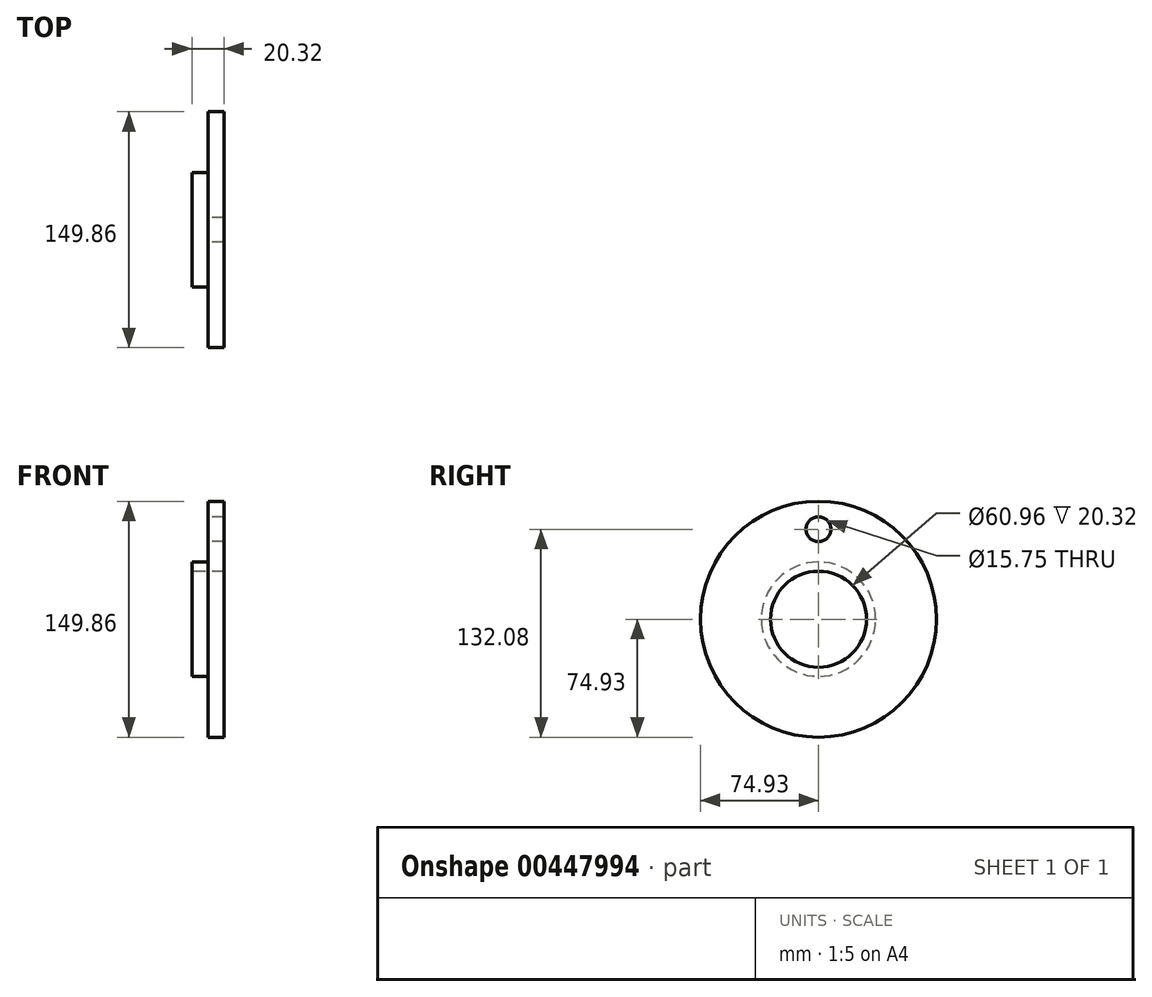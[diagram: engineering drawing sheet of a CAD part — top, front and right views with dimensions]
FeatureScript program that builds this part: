
annotation { "Feature Type Name" : "Feature", "Feature Type Description" : "" }
export const myFeature = defineFeature(function(context is Context, id is Id, definition is map)
    precondition{}
    {
        {
            var Q0;
            Q0=qCreatedBy(makeId("Front.planeOp"),FACE);
            var sketch = newSketch(context, id + "F0", { "sketchPlane" : qUnion([Q0])});
            skLineSegment(sketch, "E0", {"start": v(-98.75, 0) * mm, "end": v(111.7, 0) * mm, "construction": true});
            skSolve(sketch);
        }
        {
            var Q0;
            Q0=qCreatedBy(makeId("Front.planeOp"),FACE);
            var sketch = newSketch(context, id + "F1", { "sketchPlane" : qUnion([Q0])});
            skLineSegment(sketch, "E1", {"start": v(0, 30.48) * mm, "end": v(0, 36.32) * mm});
            skLineSegment(sketch, "E2", {"start": v(0, 36.32) * mm, "end": v(10.16, 36.32) * mm});
            skLineSegment(sketch, "E3", {"start": v(10.16, 36.32) * mm, "end": v(10.16, 74.93) * mm});
            skLineSegment(sketch, "E4", {"start": v(10.16, 74.93) * mm, "end": v(20.32, 74.93) * mm});
            skLineSegment(sketch, "E5", {"start": v(20.32, 74.93) * mm, "end": v(20.32, 30.48) * mm});
            skLineSegment(sketch, "E6", {"start": v(20.32, 30.48) * mm, "end": v(0, 30.48) * mm});
            skSolve(sketch);
        }
        {
            var Q0;
            Q0=makeQuery(id+"F1.imprint","IMPRINT",FACE,{"disambiguationData":[TD([[makeQuery(id+"F1.imprint","IMPRINT",EDGE,{"derivedFrom":sQuery(id+"F1.wireOp",EDGE,"E1")}),-1.0]])]});
            var Q1;
            Q1=sQuery(id+"F0.wireOp",EDGE,"E0");
            revolve(context, id + "F2", {"entities" : qUnion([Q0]), "axis" : qUnion([Q1]), "revolveType" : RevolveType.FULL});
        }
        {
            var Q0;
            Q0=makeQuery(id+"F2.opRevolve","SWEPT_FACE",FACE,{"disambiguationData":[OSD([sQuery(id+"F1.wireOp",EDGE,"E3")])]});
            var sketch = newSketch(context, id + "F3", { "sketchPlane" : qUnion([Q0])});
            skCircle(sketch, "E7", {"center": v(0, 0) * mm, "radius": 57.15 * mm, "construction": true});
            skCircle(sketch, "E8", {"center": v(0, 57.15) * mm, "radius": 7.87 * mm});
            skSolve(sketch);
        }
        {
            var Q0;
            Q0 = qSketchRegion(id + "F3", true);
            extrude(context, id + "F4", {"entities" : qUnion([Q0]), "operationType" : NewBodyOperationType.REMOVE, "endBound" : BoundingType.THROUGH_ALL, "oppositeDirection" : true, "depth" : 25.4 * mm});
        }
        {
            var Q0;
            Q0=makeQuery(id+"F2.opRevolve","SWEPT_FACE",FACE,{"disambiguationData":[OSD([sQuery(id+"F1.wireOp",EDGE,"E3")])]});
            var sketch = newSketch(context, id + "F5", { "sketchPlane" : qUnion([Q0])});
            skCircle(sketch, "E9", {"center": v(0, 0) * mm, "radius": 57.15 * mm, "construction": true});
            skSolve(sketch);
        }
    });
